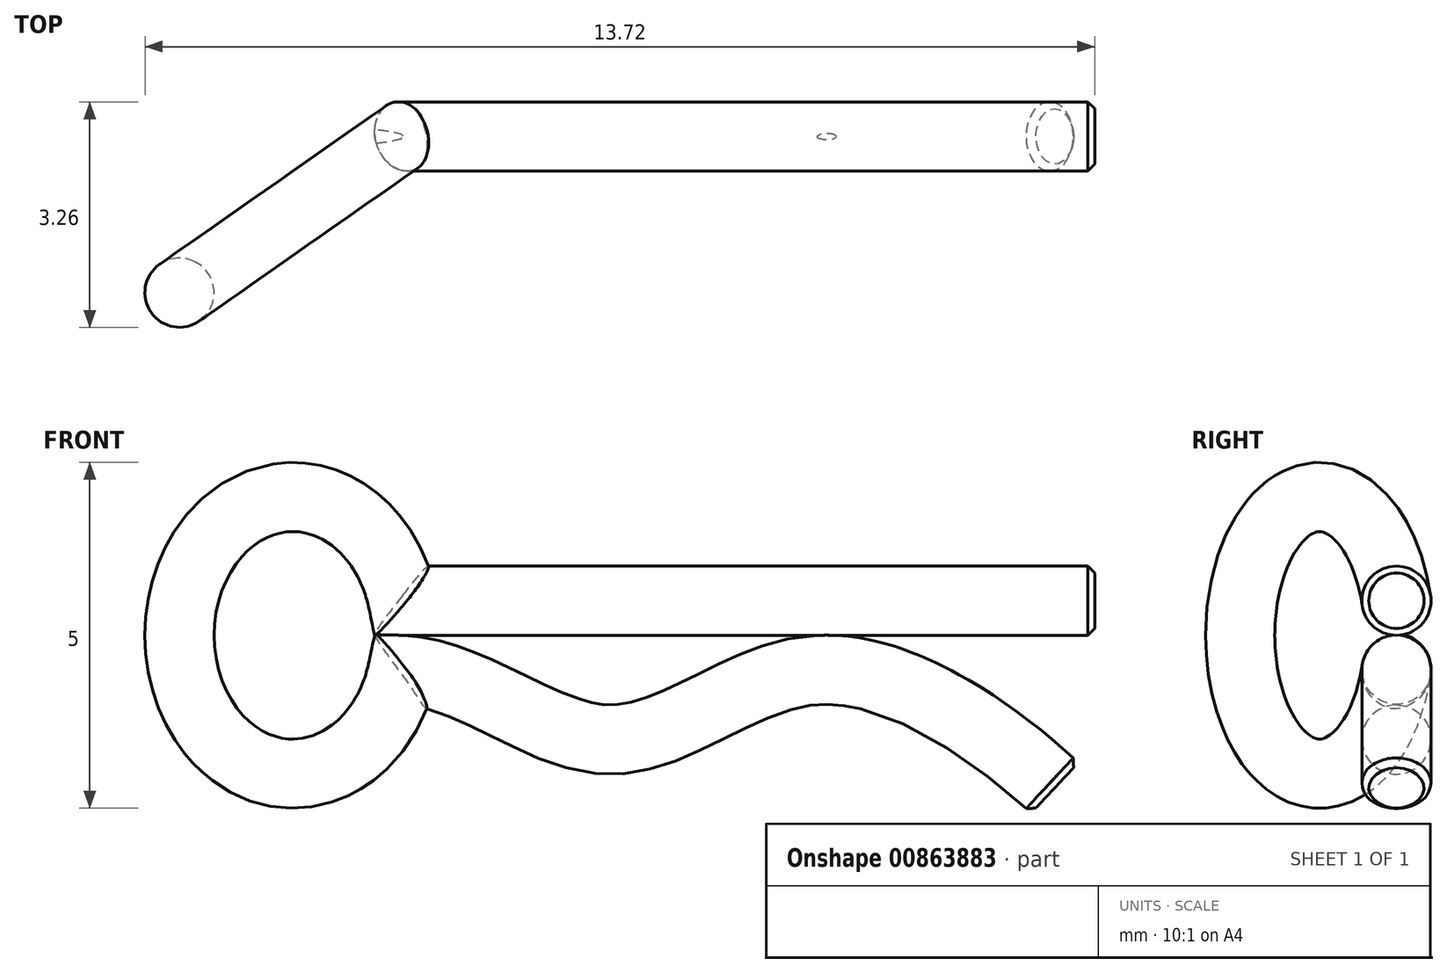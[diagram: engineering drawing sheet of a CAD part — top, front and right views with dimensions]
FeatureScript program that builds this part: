
annotation { "Feature Type Name" : "Feature", "Feature Type Description" : "" }
export const myFeature = defineFeature(function(context is Context, id is Id, definition is map)
    precondition{}
    {
        {
            var Q0;
            Q0=qCreatedBy(makeId("Front.planeOp"),FACE);
            var sketch = newSketch(context, id + "F0", { "sketchPlane" : qUnion([Q0])});
            skLineSegment(sketch, "E0", {"start": v(0, 0) * mm, "end": v(10, 0) * mm});
            skFitSpline(sketch, "E1", {"points": [v(0, -1) * mm, v(3, -2) * mm, v(6, -1) * mm, v(9.42, -2.7) * mm], "startDerivative": vector(9.7, -0.47) * mm, "endDerivative": vector(7.02, -6.56) * mm});
            skSolve(sketch);
        }
        {
            var Q0;
            Q0=qCreatedBy(makeId("Front.planeOp"),FACE);
            var sketch = newSketch(context, id + "F1", { "sketchPlane" : qUnion([Q0])});
            skLineSegment(sketch, "E2", {"start": v(0, 0) * mm, "end": v(0, -3.6) * mm});
            skSolve(sketch);
        }
        {
            var Q0;
            Q0=qCreatedBy(makeId("Front.planeOp"),FACE);
            var Q1;
            Q1=sQuery(id+"F1.wireOp",EDGE,"E2");
            cPlane(context, id + "F2", {"entities" : qUnion([Q0, Q1]), "cplaneType" : CPlaneType.LINE_ANGLE, "offset" : 25.4 * mm, "angle" : 35 * degree, "oppositeDirection" : true, "width" : 152.4 * mm, "height" : 152.4 * mm});
        }
        {
            var Q0;
            Q0=qCreatedBy(id+"F2.planeOp",FACE);
            var sketch = newSketch(context, id + "F3", { "sketchPlane" : qUnion([Q0])});
            skArc(sketch, "E3", {"start": v(0, -1) * mm, "mid": v(3.94, -0.5) * mm, "end": v(0, 0) * mm});
            skSolve(sketch);
        }
        {
            var Q0;
            Q0=qCreatedBy(makeId("Right.planeOp"),FACE);
            var sketch = newSketch(context, id + "F4", { "sketchPlane" : qUnion([Q0])});
            skCircle(sketch, "E4", {"center": v(0, 0) * mm, "radius": 0.5 * mm});
            skSolve(sketch);
        }
        {
            var Q0;
            Q0=makeQuery(id+"F4.imprint","IMPRINT",FACE,{"disambiguationData":[TD([[makeQuery(id+"F4.imprint","IMPRINT",EDGE,{"derivedFrom":sQuery(id+"F4.wireOp",EDGE,"E4")}),1.0]])]});
            var Q1;
            Q1=sQuery(id+"F0.wireOp",EDGE,"E0");
            var Q2;
            Q2=sQuery(id+"F3.wireOp",EDGE,"E3");
            var Q3;
            Q3=sQuery(id+"F0.wireOp",EDGE,"E1");
            sweep(context, id + "F5", {"profiles" : qUnion([Q0]), "path" : qUnion([Q1, Q2, Q3])});
        }
        {
            var Q0;
            Q0=makeQuery(id+"F5.opSweep","CAP_EDGE",EDGE,{"disambiguationData":[OSD([sQuery(id+"F0.wireOp",VERTEX,"E0.end"),sQuery(id+"F4.wireOp",EDGE,"E4")])],"isStart":false});
            var Q1;
            Q1=makeQuery(id+"F5.opSweep","CAP_EDGE",EDGE,{"disambiguationData":[OSD([sQuery(id+"F0.wireOp",VERTEX,"E1.end"),sQuery(id+"F4.wireOp",EDGE,"E4")])],"isStart":true});
            chamfer(context, id + "F6", {"entities" : qUnion([Q0, Q1]), "width" : .1 * mm, "tangentPropagation" : true});
        }
    });
